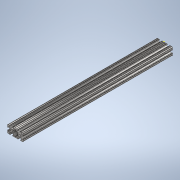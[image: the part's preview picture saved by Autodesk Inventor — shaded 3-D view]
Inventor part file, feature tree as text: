
AUTODESK INVENTOR PART (.ipt)
format: ipt  version: 2020 (Build 240168000, 168)  size: 348,160 bytes
history: native  units: in
note: dims shown in document units (in); Inventor stores cm internally (conversion verified against a paired STEP export)
features: sketch x2, extrude x1
ambient origin geometry x8: Origin, YZ Plane, XZ Plane, XY Plane, X Axis, Y Axis, Z Axis, Center Point
bodies: Solid1 (feature_tree)
feature tree (3):
  extrude  "Extrusion1"  [1 undecoded]
  sketch  "Sketch2"
  sketch  "Sketch1"  dims[d0=19.0in d1=0.0in]
note: 1 required parameter value undecoded (feature->parameter linkage not recoverable at this tier; creation-order binding heuristic only, values carry confidence <= 0.55)
